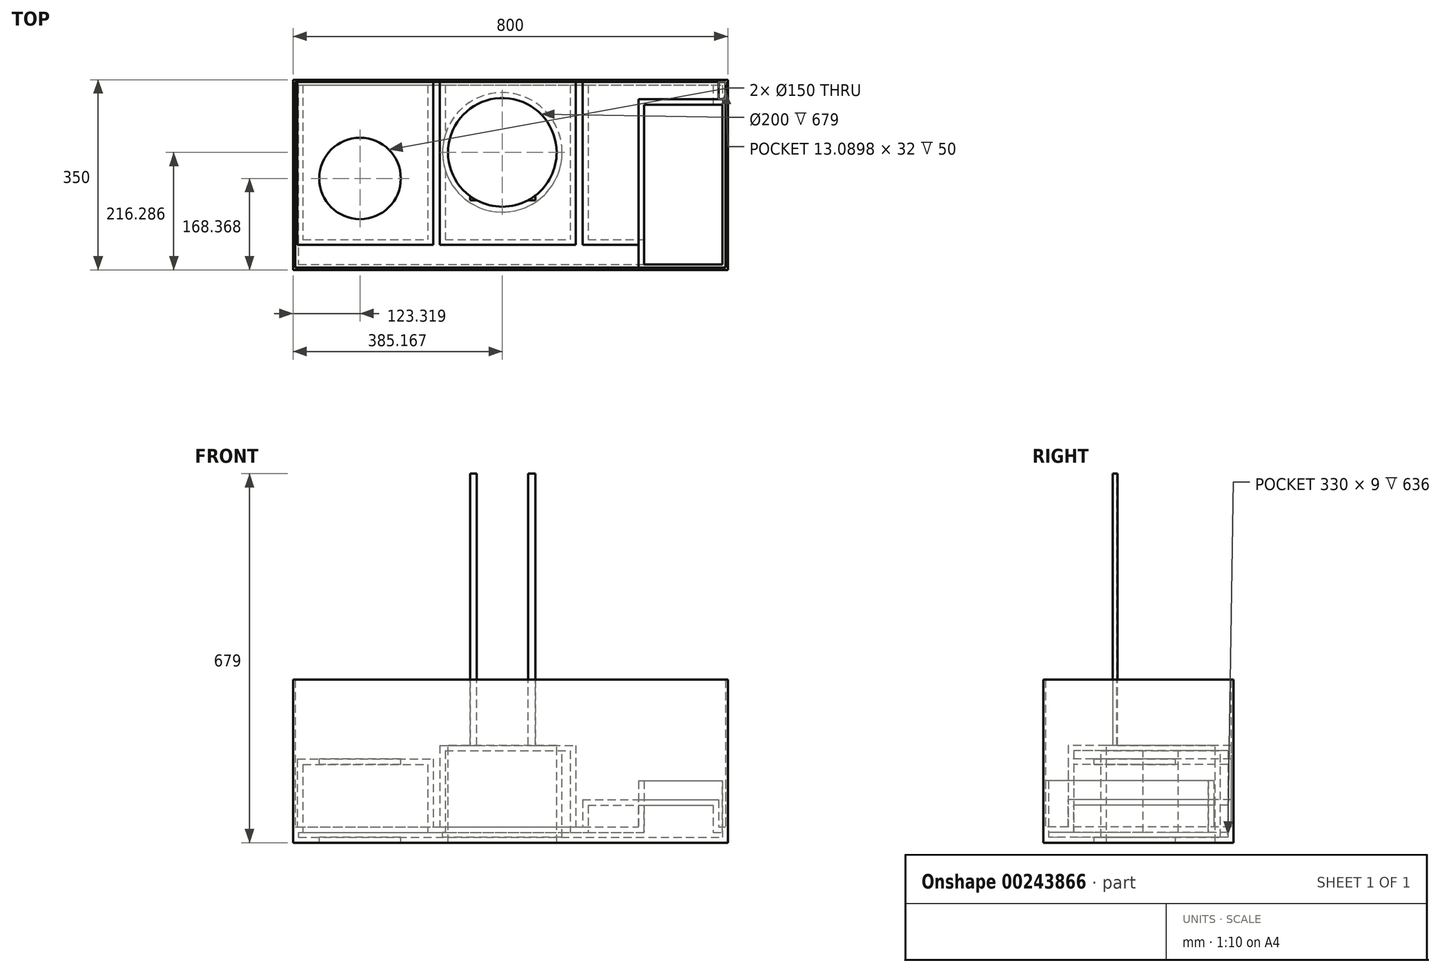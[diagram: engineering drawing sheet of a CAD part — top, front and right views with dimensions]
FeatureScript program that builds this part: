
annotation { "Feature Type Name" : "Feature", "Feature Type Description" : "" }
export const myFeature = defineFeature(function(context is Context, id is Id, definition is map)
    precondition{}
    {
        {
            var Q0;
            Q0=qCreatedBy(makeId("Top.planeOp"),FACE);
            var sketch = newSketch(context, id + "F0", { "sketchPlane" : qUnion([Q0])});
            skLineSegment(sketch, "E0.bottom", {"start": v(0, 0) * mm, "end": v(800, 0) * mm});
            skLineSegment(sketch, "E0.top", {"start": v(0, -350) * mm, "end": v(800, -350) * mm});
            skLineSegment(sketch, "E0.left", {"start": v(0, 0) * mm, "end": v(0, -350) * mm});
            skLineSegment(sketch, "E0.right", {"start": v(800, 0) * mm, "end": v(800, -350) * mm});
            skSolve(sketch);
        }
        {
            var Q0;
            Q0=makeQuery(id+"F0.imprint","IMPRINT",FACE,{"disambiguationData":[TD([[makeQuery(id+"F0.imprint","IMPRINT",EDGE,{"derivedFrom":sQuery(id+"F0.wireOp",EDGE,"E0.bottom")}),-1.0]])]});
            extrude(context, id + "F1", {"entities" : qUnion([Q0]), "depth" : 300 * mm});
        }
        {
            var Q0;
            Q0=makeQuery(id+"F1.opExtrude","CAP_FACE",FACE,{"disambiguationData":[OSD([sQuery(id+"F0.wireOp",EDGE,"E0.bottom"),sQuery(id+"F0.wireOp",EDGE,"E0.top"),sQuery(id+"F0.wireOp",EDGE,"E0.left"),sQuery(id+"F0.wireOp",EDGE,"E0.right")])],"isStart":false});
            shell(context, id + "F2", {"entities" : qUnion([Q0]), "thickness" : 4 * mm});
        }
        {
            var Q0;
            Q0=makeQuery(id+"F2.opShell","OFFSET_FACE",FACE,{"disambiguationData":[OSD([sQuery(id+"F0.wireOp",EDGE,"E0.bottom"),sQuery(id+"F0.wireOp",EDGE,"E0.top"),sQuery(id+"F0.wireOp",EDGE,"E0.left"),sQuery(id+"F0.wireOp",EDGE,"E0.right")])]});
            var sketch = newSketch(context, id + "F3", { "sketchPlane" : qUnion([Q0])});
            skLineSegment(sketch, "E1.bottom", {"start": v(7.94, -4) * mm, "end": v(257.94, -4) * mm});
            skLineSegment(sketch, "E1.top", {"start": v(7.94, -304) * mm, "end": v(257.94, -304) * mm});
            skLineSegment(sketch, "E1.left", {"start": v(7.94, -4) * mm, "end": v(7.94, -304) * mm});
            skLineSegment(sketch, "E1.right", {"start": v(257.94, -4) * mm, "end": v(257.94, -304) * mm});
            skSolve(sketch);
        }
        {
            var Q0;
            Q0 = qSketchRegion(id + "F3", true);
            extrude(context, id + "F4", {"entities" : qUnion([Q0]), "operationType" : NewBodyOperationType.ADD, "depth" : 150 * mm});
        }
        {
            var Q0;
            Q0=makeQuery(id+"F2.opShell","OFFSET_FACE",FACE,{"disambiguationData":[OSD([sQuery(id+"F0.wireOp",EDGE,"E0.bottom"),sQuery(id+"F0.wireOp",EDGE,"E0.top"),sQuery(id+"F0.wireOp",EDGE,"E0.left"),sQuery(id+"F0.wireOp",EDGE,"E0.right")])]});
            var sketch = newSketch(context, id + "F5", { "sketchPlane" : qUnion([Q0])});
            skLineSegment(sketch, "E2.bottom", {"start": v(636, -36) * mm, "end": v(796, -36) * mm});
            skLineSegment(sketch, "E2.top", {"start": v(636, -346) * mm, "end": v(796, -346) * mm});
            skLineSegment(sketch, "E2.left", {"start": v(636, -36) * mm, "end": v(636, -346) * mm});
            skLineSegment(sketch, "E2.right", {"start": v(796, -36) * mm, "end": v(796, -346) * mm});
            skSolve(sketch);
        }
        {
            var Q0;
            Q0 = qSketchRegion(id + "F5", true);
            extrude(context, id + "F6", {"entities" : qUnion([Q0]), "operationType" : NewBodyOperationType.ADD, "depth" : 110 * mm});
        }
        {
            var Q0;
            Q0=makeQuery(id+"F3.imprint","IMPRINT",FACE,{"disambiguationData":[TD([[makeQuery(id+"F3.imprint","IMPRINT",EDGE,{"derivedFrom":sQuery(id+"F3.wireOp",EDGE,"E1.top")}),-1.0]])]});
            extrude(context, id + "F7", {"entities" : qUnion([Q0]), "operationType" : NewBodyOperationType.ADD, "depth" : 25 * mm});
        }
        {
            var Q0;
            Q0=makeQuery(id+"F7.opExtrude","CAP_FACE",FACE,{"disambiguationData":[OSD([sQuery(id+"F0.wireOp",EDGE,"E0.bottom"),sQuery(id+"F0.wireOp",EDGE,"E0.top"),sQuery(id+"F0.wireOp",EDGE,"E0.left"),sQuery(id+"F0.wireOp",EDGE,"E0.right"),sQuery(id+"F3.wireOp",EDGE,"E1.top"),sQuery(id+"F3.wireOp",EDGE,"E1.left"),sQuery(id+"F3.wireOp",EDGE,"E1.right")])],"isStart":false});
            var sketch = newSketch(context, id + "F8", { "sketchPlane" : qUnion([Q0])});
            skLineSegment(sketch, "E3.bottom", {"start": v(270, -4) * mm, "end": v(520, -4) * mm});
            skLineSegment(sketch, "E3.top", {"start": v(270, -304) * mm, "end": v(520, -304) * mm});
            skLineSegment(sketch, "E3.left", {"start": v(270, -4) * mm, "end": v(270, -304) * mm});
            skLineSegment(sketch, "E3.right", {"start": v(520, -4) * mm, "end": v(520, -304) * mm});
            skSolve(sketch);
        }
        {
            var Q0;
            Q0 = qSketchRegion(id + "F8", true);
            extrude(context, id + "F9", {"entities" : qUnion([Q0]), "operationType" : NewBodyOperationType.ADD, "depth" : 150 * mm});
        }
        {
            var Q0;
            Q0=makeQuery(id+"F7.opExtrude","CAP_FACE",FACE,{"disambiguationData":[OSD([sQuery(id+"F0.wireOp",EDGE,"E0.bottom"),sQuery(id+"F0.wireOp",EDGE,"E0.top"),sQuery(id+"F0.wireOp",EDGE,"E0.left"),sQuery(id+"F0.wireOp",EDGE,"E0.right"),sQuery(id+"F3.wireOp",EDGE,"E1.top"),sQuery(id+"F3.wireOp",EDGE,"E1.left"),sQuery(id+"F3.wireOp",EDGE,"E1.right")])],"isStart":false});
            var sketch = newSketch(context, id + "F10", { "sketchPlane" : qUnion([Q0])});
            skLineSegment(sketch, "E4.bottom", {"start": v(532.91, -4) * mm, "end": v(782.91, -4) * mm});
            skLineSegment(sketch, "E4.top", {"start": v(532.91, -304) * mm, "end": v(782.91, -304) * mm});
            skLineSegment(sketch, "E4.left", {"start": v(532.91, -4) * mm, "end": v(532.91, -304) * mm});
            skLineSegment(sketch, "E4.right", {"start": v(782.91, -4) * mm, "end": v(782.91, -304) * mm});
            skSolve(sketch);
        }
        {
            var Q0;
            Q0 = qSketchRegion(id + "F10", true);
            extrude(context, id + "F11", {"entities" : qUnion([Q0]), "operationType" : NewBodyOperationType.ADD, "depth" : 50 * mm});
        }
        {
            var Q0;
            Q0=makeQuery(id+"F9.opExtrude","CAP_FACE",FACE,{"disambiguationData":[OSD([sQuery(id+"F8.wireOp",EDGE,"E3.bottom"),sQuery(id+"F8.wireOp",EDGE,"E3.top"),sQuery(id+"F8.wireOp",EDGE,"E3.left"),sQuery(id+"F8.wireOp",EDGE,"E3.right")])],"isStart":false});
            var sketch = newSketch(context, id + "F12", { "sketchPlane" : qUnion([Q0])});
            skLineSegment(sketch, "E5.bottom", {"start": v(325.82, -71.8) * mm, "end": v(445.82, -71.8) * mm});
            skLineSegment(sketch, "E5.top", {"start": v(325.82, -221.8) * mm, "end": v(445.82, -221.8) * mm});
            skLineSegment(sketch, "E5.left", {"start": v(325.82, -71.8) * mm, "end": v(325.82, -221.8) * mm});
            skLineSegment(sketch, "E5.right", {"start": v(445.82, -71.8) * mm, "end": v(445.82, -221.8) * mm});
            skSolve(sketch);
        }
        {
            var Q0;
            Q0=makeQuery(id+"F12.imprint","IMPRINT",FACE,{"disambiguationData":[TD([[makeQuery(id+"F12.imprint","IMPRINT",EDGE,{"derivedFrom":sQuery(id+"F12.wireOp",EDGE,"E5.bottom")}),-1.0]])]});
            extrude(context, id + "F13", {"entities" : qUnion([Q0]), "operationType" : NewBodyOperationType.ADD, "depth" : 500 * mm});
        }
        {
            var Q0;
            Q0=makeQuery(id+"F13.opExtrude","CAP_FACE",FACE,{"disambiguationData":[OSD([sQuery(id+"F12.wireOp",EDGE,"E5.bottom"),sQuery(id+"F12.wireOp",EDGE,"E5.top"),sQuery(id+"F12.wireOp",EDGE,"E5.left"),sQuery(id+"F12.wireOp",EDGE,"E5.right")])],"isStart":false});
            var sketch = newSketch(context, id + "F14", { "sketchPlane" : qUnion([Q0])});
            skCircle(sketch, "E6", {"center": v(385.17, -133.71) * mm, "radius": 42.93 * mm});
            skSolve(sketch);
        }
        {
            var Q0;
            Q0=sQuery(id+"F14.wireOp",VERTEX,"E6.center");
            var Q1;
            Q1=makeQuery(id+"F1.opExtrude","SWEPT_BODY",BODY,{"disambiguationData":[OSD([sQuery(id+"F0.wireOp",EDGE,"E0.bottom"),sQuery(id+"F0.wireOp",EDGE,"E0.top"),sQuery(id+"F0.wireOp",EDGE,"E0.left"),sQuery(id+"F0.wireOp",EDGE,"E0.right")])]});
            hole(context, id + "F15", {"style" : HoleStyle.SIMPLE, "endStyle" : HoleEndStyle.THROUGH, "holeDiameter" : 200 * mm, "tappedDepth" : 12 * mm, "tapClearance" : 3, "locations" : qUnion([Q0]), "scope" : qUnion([Q1])});
        }
        {
            var Q0;
            Q0=makeQuery(id+"F15.hole-0.boolean.opBoolean","COPY",FACE,{"derivedFrom":makeQuery(id+"F15.hole-0.opRevolve","SWEPT_FACE",FACE,{"disambiguationData":[OSD([sQuery(id+"F15.hole-0.sketch.wireOp",EDGE,"core_line_2")])]})});
            var Q1;
            Q1=makeQuery(id+"F6.opExtrude","CAP_FACE",FACE,{"disambiguationData":[OSD([sQuery(id+"F5.wireOp",EDGE,"E2.bottom"),sQuery(id+"F5.wireOp",EDGE,"E2.top"),sQuery(id+"F5.wireOp",EDGE,"E2.left"),sQuery(id+"F5.wireOp",EDGE,"E2.right")])],"isStart":false});
            shell(context, id + "F16", {"entities" : qUnion([Q0, Q1]), "thickness" : 10 * mm});
        }
        {
            var Q0;
            Q0=makeQuery(id+"F4.opExtrude","CAP_FACE",FACE,{"disambiguationData":[OSD([sQuery(id+"F3.wireOp",EDGE,"E1.bottom"),sQuery(id+"F3.wireOp",EDGE,"E1.top"),sQuery(id+"F3.wireOp",EDGE,"E1.left"),sQuery(id+"F3.wireOp",EDGE,"E1.right")])],"isStart":false});
            var sketch = newSketch(context, id + "F17", { "sketchPlane" : qUnion([Q0])});
            skPoint(sketch, "E7", {"position": v(123.32, -181.63) * mm});
            skSolve(sketch);
        }
        {
            var Q0;
            Q0=sQuery(id+"F17.wireOp",VERTEX,"E7");
            var Q1;
            Q1=makeQuery(id+"F1.opExtrude","SWEPT_BODY",BODY,{"disambiguationData":[OSD([sQuery(id+"F0.wireOp",EDGE,"E0.bottom"),sQuery(id+"F0.wireOp",EDGE,"E0.top"),sQuery(id+"F0.wireOp",EDGE,"E0.left"),sQuery(id+"F0.wireOp",EDGE,"E0.right")])]});
            hole(context, id + "F18", {"style" : HoleStyle.SIMPLE, "endStyle" : HoleEndStyle.THROUGH, "holeDiameter" : 150 * mm, "tappedDepth" : 12 * mm, "tapClearance" : 3, "locations" : qUnion([Q0]), "scope" : qUnion([Q1])});
        }
    });
